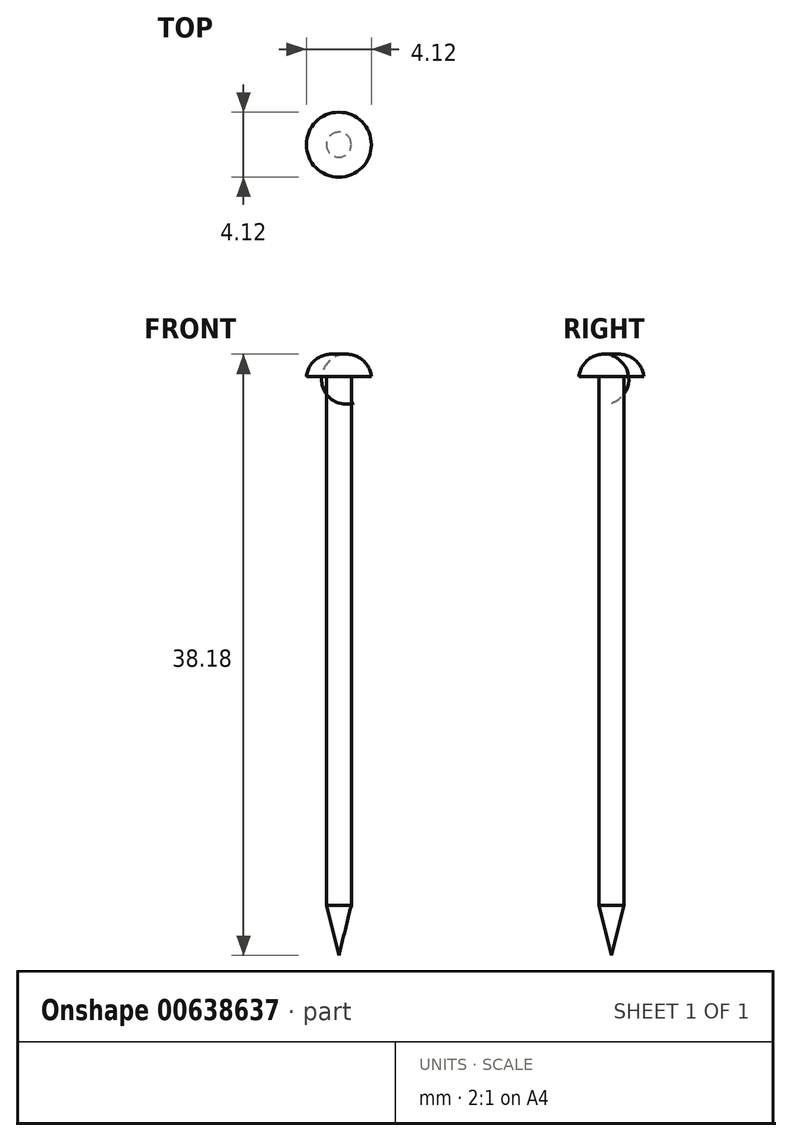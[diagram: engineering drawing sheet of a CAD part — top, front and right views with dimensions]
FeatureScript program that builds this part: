
annotation { "Feature Type Name" : "Feature", "Feature Type Description" : "" }
export const myFeature = defineFeature(function(context is Context, id is Id, definition is map)
    precondition{}
    {
        {
            var Q0;
            Q0=qCreatedBy(makeId("Front.planeOp"),FACE);
            var sketch = newSketch(context, id + "F0", { "sketchPlane" : qUnion([Q0])});
            skLineSegment(sketch, "E0", {"start": v(0, -27.94) * mm, "end": v(-0.8, -24.76) * mm});
            skLineSegment(sketch, "E1", {"start": v(-0.8, -24.76) * mm, "end": v(0, -24.76) * mm});
            skLineSegment(sketch, "E2", {"start": v(0, -24.76) * mm, "end": v(0, -27.94) * mm});
            skLineSegment(sketch, "E3", {"start": v(-0.8, -24.76) * mm, "end": v(-0.8, 8.81) * mm});
            skLineSegment(sketch, "E4", {"start": v(-0.8, 8.81) * mm, "end": v(-2.06, 8.81) * mm});
            skLineSegment(sketch, "E5", {"start": v(0, -24.76) * mm, "end": v(0, 10.16) * mm});
            skArc(sketch, "E6", {"start": v(0, 10.16) * mm, "mid": v(-1.35, 9.98) * mm, "end": v(-2.06, 8.81) * mm});
            skLineSegment(sketch, "E7", {"start": v(0, 14.74) * mm, "end": v(0, -32.63) * mm, "construction": true});
            skSolve(sketch);
        }
        {
            var Q0;
            Q0 = qSketchRegion(id + "F0", true);
            var Q1;
            Q1=sQuery(id+"F0.wireOp",EDGE,"E7");
            revolve(context, id + "F1", {"entities" : qUnion([Q0]), "axis" : qUnion([Q1]), "revolveType" : RevolveType.FULL});
        }
    });
